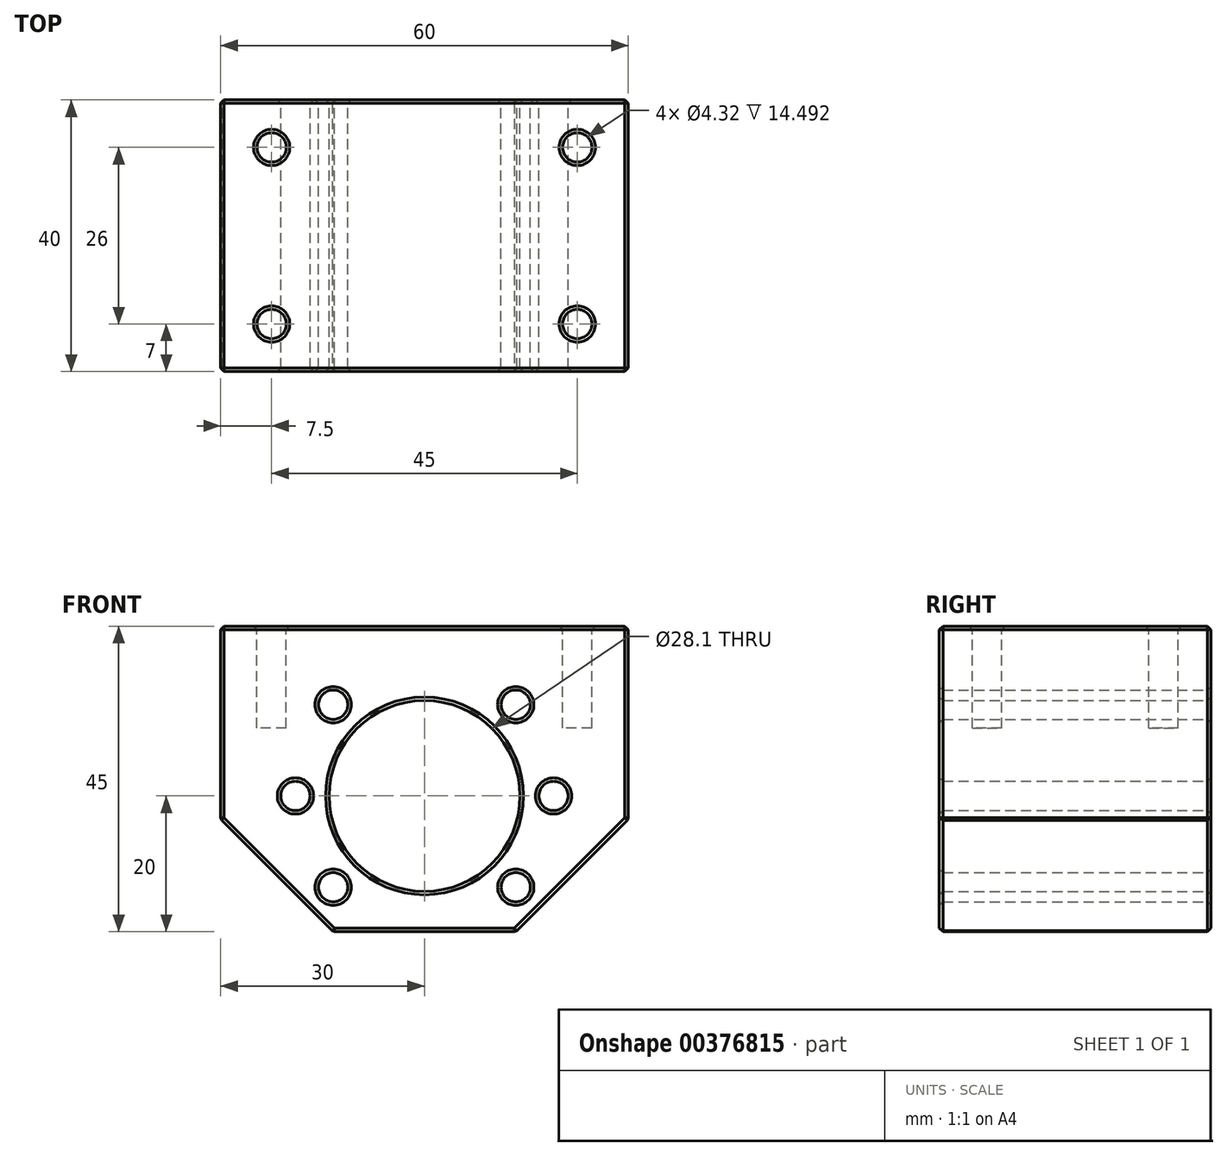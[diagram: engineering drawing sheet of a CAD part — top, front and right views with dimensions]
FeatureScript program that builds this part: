
annotation { "Feature Type Name" : "Feature", "Feature Type Description" : "" }
export const myFeature = defineFeature(function(context is Context, id is Id, definition is map)
    precondition{}
    {
        {
            var Q0;
            Q0=qCreatedBy(makeId("Front.planeOp"),FACE);
            var sketch = newSketch(context, id + "F0", { "sketchPlane" : qUnion([Q0])});
            skLineSegment(sketch, "E0.bottom", {"start": v(30, 22.5) * mm, "end": v(-30, 22.5) * mm});
            skLineSegment(sketch, "E0.top", {"start": v(30, -22.5) * mm, "end": v(-30, -22.5) * mm});
            skLineSegment(sketch, "E0.left", {"start": v(30, 22.5) * mm, "end": v(30, -22.5) * mm});
            skLineSegment(sketch, "E0.right", {"start": v(-30, 22.5) * mm, "end": v(-30, -22.5) * mm});
            skPoint(sketch, "E0.middle", {"position": v(0, 0) * mm});
            skCircle(sketch, "E1", {"center": v(0, -2.5) * mm, "radius": 14.05 * mm});
            skCircle(sketch, "E2", {"center": v(-13.44, -15.94) * mm, "radius": 2.16 * mm});
            skCircle(sketch, "E3", {"center": v(-13.44, 10.94) * mm, "radius": 2.16 * mm});
            skCircle(sketch, "E4", {"center": v(-19, -2.5) * mm, "radius": 2.16 * mm});
            skCircle(sketch, "E5", {"center": v(19, -2.5) * mm, "radius": 2.16 * mm});
            skCircle(sketch, "E6", {"center": v(13.44, 10.94) * mm, "radius": 2.16 * mm});
            skCircle(sketch, "E7", {"center": v(13.44, -15.94) * mm, "radius": 2.16 * mm});
            skLineSegment(sketch, "E8", {"start": v(30, -5.94) * mm, "end": v(13.44, -22.5) * mm, "construction": true});
            skLineSegment(sketch, "E9", {"start": v(-30, -5.94) * mm, "end": v(-13.44, -22.5) * mm, "construction": true});
            skLineSegment(sketch, "E10", {"start": v(-30, -5.94) * mm, "end": v(-13.44, -22.5) * mm});
            skLineSegment(sketch, "E11", {"start": v(30, -5.94) * mm, "end": v(13.44, -22.5) * mm});
            skSolve(sketch);
        }
        {
            var Q0;
            {var subQ0=sQuery(id+"F0.wireOp",EDGE,"E0.bottom");Q0=makeQuery(id+"F0.imprint","IMPRINT",FACE,{"disambiguationData":[TD([[makeQuery(id+"F0.imprint","IMPRINT",EDGE,{"derivedFrom":subQ0}),1.0]])]});}
            extrude(context, id + "F1", {"entities" : qUnion([Q0]), "depth" : 40 * mm});
        }
        {
            var Q0;
            Q0=makeQuery(id+"F1.opExtrude","SWEPT_FACE",FACE,{"disambiguationData":[OSD([sQuery(id+"F0.wireOp",EDGE,"E0.bottom")])]});
            var sketch = newSketch(context, id + "F2", { "sketchPlane" : qUnion([Q0])});
            skCircle(sketch, "E12", {"center": v(-22.5, -33) * mm, "radius": 2.16 * mm});
            skCircle(sketch, "E13", {"center": v(-22.5, -7) * mm, "radius": 2.16 * mm});
            skCircle(sketch, "E14", {"center": v(22.5, -7) * mm, "radius": 2.16 * mm});
            skCircle(sketch, "E15", {"center": v(22.5, -33) * mm, "radius": 2.16 * mm});
            skLineSegment(sketch, "E16", {"start": v(-30, -20) * mm, "end": v(30, -20) * mm, "construction": true});
            skLineSegment(sketch, "E17", {"start": v(0, 0) * mm, "end": v(0, -40) * mm, "construction": true});
            skSolve(sketch);
        }
        {
            var Q0;
            Q0=makeQuery(id+"F2.imprint","IMPRINT",FACE,{"disambiguationData":[TD([[makeQuery(id+"F2.imprint","IMPRINT",EDGE,{"derivedFrom":sQuery(id+"F2.wireOp",EDGE,"E13")}),1.0]])]});
            var Q1;
            Q1=makeQuery(id+"F2.imprint","IMPRINT",FACE,{"disambiguationData":[TD([[makeQuery(id+"F2.imprint","IMPRINT",EDGE,{"derivedFrom":sQuery(id+"F2.wireOp",EDGE,"E14")}),1.0]])]});
            var Q2;
            Q2=makeQuery(id+"F2.imprint","IMPRINT",FACE,{"disambiguationData":[TD([[makeQuery(id+"F2.imprint","IMPRINT",EDGE,{"derivedFrom":sQuery(id+"F2.wireOp",EDGE,"E12")}),1.0]])]});
            var Q3;
            Q3=makeQuery(id+"F2.imprint","IMPRINT",FACE,{"disambiguationData":[TD([[makeQuery(id+"F2.imprint","IMPRINT",EDGE,{"derivedFrom":sQuery(id+"F2.wireOp",EDGE,"E15")}),1.0]])]});
            extrude(context, id + "F3", {"entities" : qUnion([Q0, Q1, Q2, Q3]), "operationType" : NewBodyOperationType.REMOVE, "oppositeDirection" : true, "depth" : 15 * mm});
        }
        {
            var Q0;
            Q0=makeQuery(id+"F1.opExtrude","CAP_FACE",FACE,{"disambiguationData":[OSD([sQuery(id+"F0.wireOp",EDGE,"E0.bottom"),sQuery(id+"F0.wireOp",EDGE,"E0.top"),sQuery(id+"F0.wireOp",EDGE,"E0.left"),sQuery(id+"F0.wireOp",EDGE,"E0.right"),sQuery(id+"F0.wireOp",EDGE,"E1"),sQuery(id+"F0.wireOp",EDGE,"E2"),sQuery(id+"F0.wireOp",EDGE,"E3"),sQuery(id+"F0.wireOp",EDGE,"E4"),sQuery(id+"F0.wireOp",EDGE,"E5"),sQuery(id+"F0.wireOp",EDGE,"E6"),sQuery(id+"F0.wireOp",EDGE,"E7"),sQuery(id+"F0.wireOp",EDGE,"E10"),sQuery(id+"F0.wireOp",EDGE,"E11")])],"isStart":false});
            var Q1;
            Q1=makeQuery(id+"F1.opExtrude","SWEPT_FACE",FACE,{"disambiguationData":[OSD([sQuery(id+"F0.wireOp",EDGE,"E0.left")])]});
            var Q2;
            Q2=makeQuery(id+"F1.opExtrude","SWEPT_FACE",FACE,{"disambiguationData":[OSD([sQuery(id+"F0.wireOp",EDGE,"E11")])]});
            var Q3;
            Q3=makeQuery(id+"F1.opExtrude","SWEPT_FACE",FACE,{"disambiguationData":[OSD([sQuery(id+"F0.wireOp",EDGE,"E10")])]});
            var Q4;
            Q4=makeQuery(id+"F1.opExtrude","SWEPT_FACE",FACE,{"disambiguationData":[OSD([sQuery(id+"F0.wireOp",EDGE,"E0.right")])]});
            var Q5;
            Q5=makeQuery(id+"F1.opExtrude","CAP_FACE",FACE,{"disambiguationData":[OSD([sQuery(id+"F0.wireOp",EDGE,"E0.bottom"),sQuery(id+"F0.wireOp",EDGE,"E0.top"),sQuery(id+"F0.wireOp",EDGE,"E0.left"),sQuery(id+"F0.wireOp",EDGE,"E0.right"),sQuery(id+"F0.wireOp",EDGE,"E1"),sQuery(id+"F0.wireOp",EDGE,"E2"),sQuery(id+"F0.wireOp",EDGE,"E3"),sQuery(id+"F0.wireOp",EDGE,"E4"),sQuery(id+"F0.wireOp",EDGE,"E5"),sQuery(id+"F0.wireOp",EDGE,"E6"),sQuery(id+"F0.wireOp",EDGE,"E7"),sQuery(id+"F0.wireOp",EDGE,"E10"),sQuery(id+"F0.wireOp",EDGE,"E11")])],"isStart":true});
            var Q6;
            Q6=makeQuery(id+"F1.opExtrude","SWEPT_FACE",FACE,{"disambiguationData":[OSD([sQuery(id+"F0.wireOp",EDGE,"E0.bottom")])]});
            chamfer(context, id + "F4", {"entities" : qUnion([Q0, Q1, Q2, Q3, Q4, Q5, Q6]), "width" : 0.5 * mm, "tangentPropagation" : true});
        }
    });
